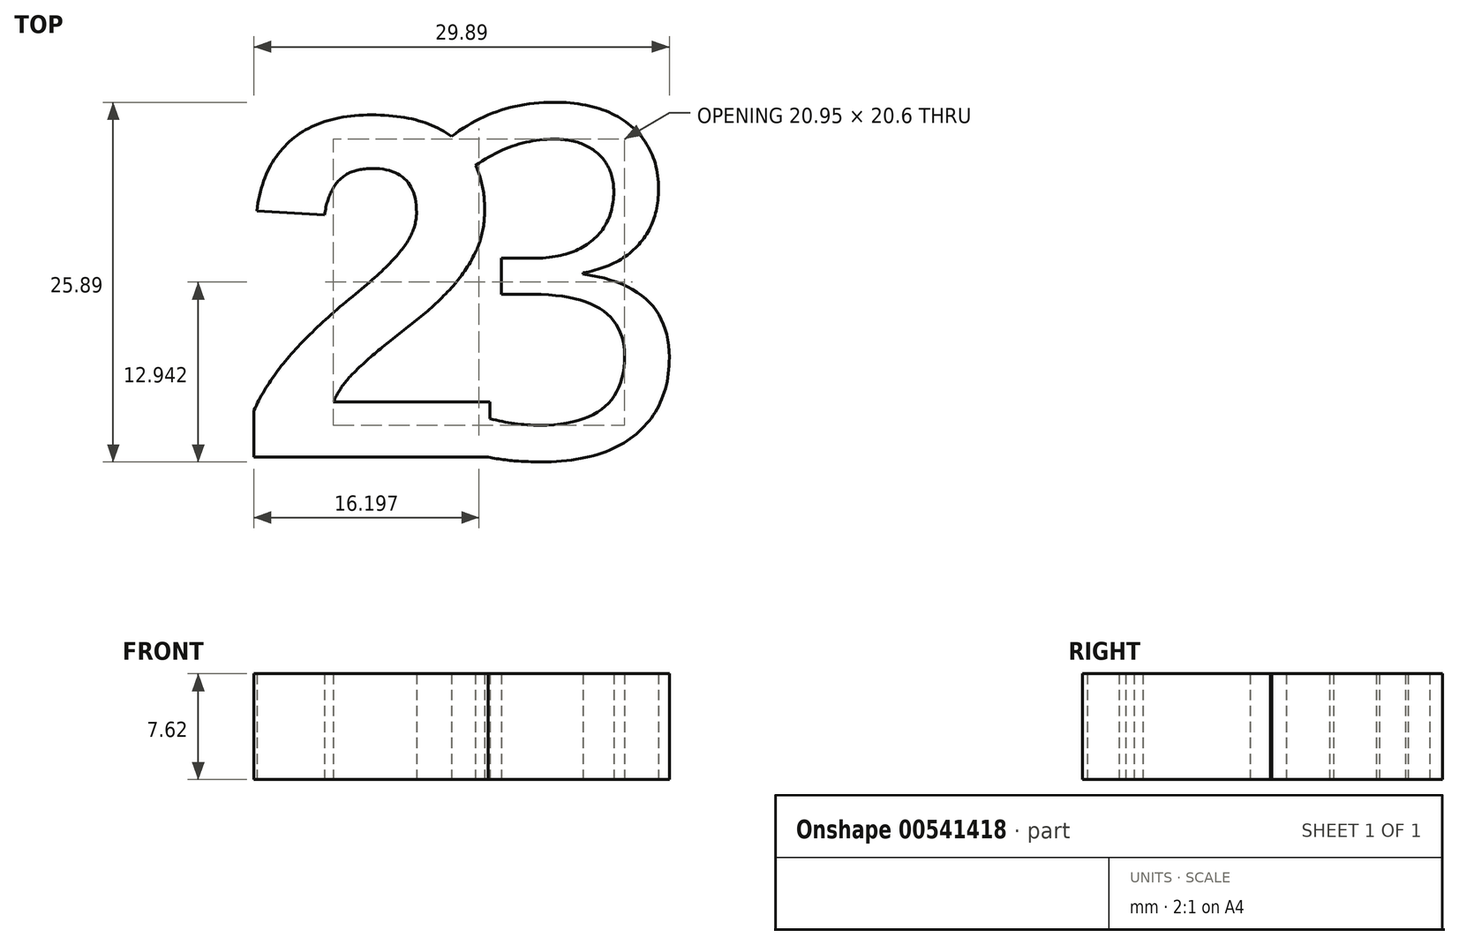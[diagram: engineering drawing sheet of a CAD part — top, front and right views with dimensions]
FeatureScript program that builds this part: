
annotation { "Feature Type Name" : "Feature", "Feature Type Description" : "" }
export const myFeature = defineFeature(function(context is Context, id is Id, definition is map)
    precondition{}
    {
        {
            var Q0;
            Q0=qCreatedBy(makeId("Top.planeOp"),FACE);
            var sketch = newSketch(context, id + "F0", { "sketchPlane" : qUnion([Q0])});
            skText(sketch, "E0", { "text": "2", "fontName": "Arimo-Bold.ttf"});
            skText(sketch, "E1", { "text": "3", "fontName": "DroidSansMono.ttf"});
            const initialGuessF0  = {"E0": [-0.02065, 0, 1, 0, 0.0254], "E1": [-0.00771, 0, 1, 0, 0.0254]};
            skSetInitialGuess(sketch, initialGuessF0);
            skSolve(sketch);
        }
        {
            var Q0;
            Q0 = qSketchRegion(id + "F0", true);
            extrude(context, id + "F1", {"entities" : qUnion([Q0]), "depth" : 7.62 * mm, "offsetDistance" : 25.4 * mm});
        }
    });
